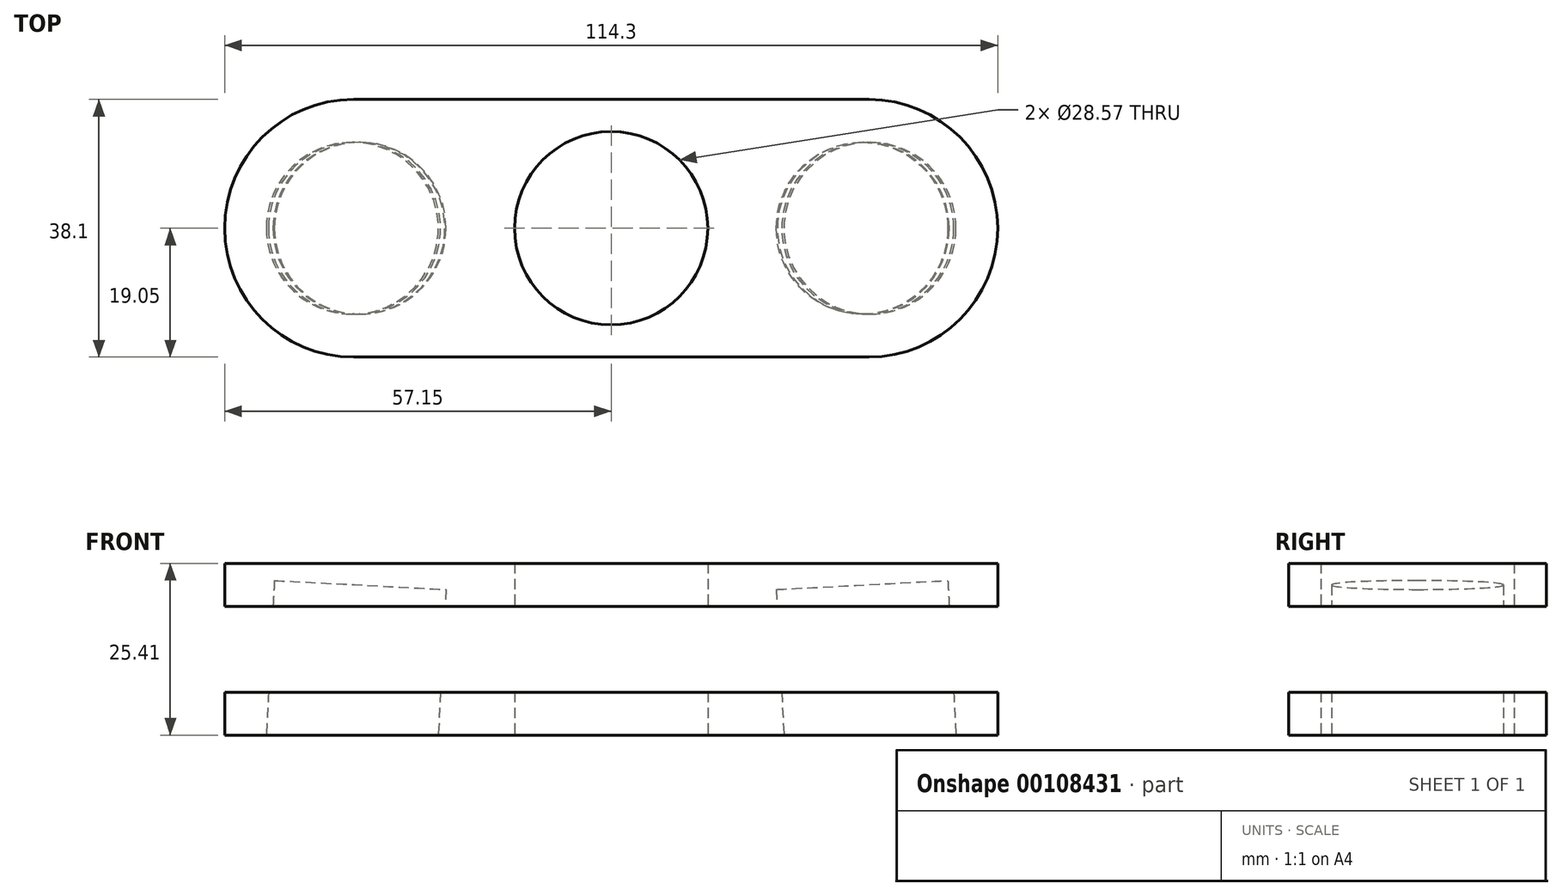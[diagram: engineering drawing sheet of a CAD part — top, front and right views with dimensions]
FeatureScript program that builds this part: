
annotation { "Feature Type Name" : "Feature", "Feature Type Description" : "" }
export const myFeature = defineFeature(function(context is Context, id is Id, definition is map)
    precondition{}
    {
        {
            var Q0;
            Q0=qCreatedBy(makeId("Top.planeOp"),FACE);
            var sketch = newSketch(context, id + "F0", { "sketchPlane" : qUnion([Q0])});
            skLineSegment(sketch, "E0.bottom", {"start": v(38.1, 19.05) * mm, "end": v(-38.1, 19.05) * mm});
            skLineSegment(sketch, "E0.top", {"start": v(38.1, -19.05) * mm, "end": v(-38.1, -19.05) * mm});
            skPoint(sketch, "E0.middle", {"position": v(0, 0) * mm});
            skArc(sketch, "E1", {"start": v(38.1, -19.05) * mm, "mid": v(57.15, 0) * mm, "end": v(38.1, 19.05) * mm});
            skArc(sketch, "E2", {"start": v(-38.1, 19.05) * mm, "mid": v(-57.15, 0) * mm, "end": v(-38.1, -19.05) * mm});
            skCircle(sketch, "E3", {"center": v(0, 0) * mm, "radius": 14.29 * mm});
            skSolve(sketch);
        }
        {
            var Q0;
            Q0 = qSketchRegion(id + "F0", true);
            extrude(context, id + "F1", {"entities" : qUnion([Q0]), "depth" : 6.35 * mm, "symmetric" : true});
        }
        {
            var Q0;
            Q0=qCreatedBy(makeId("Top.planeOp"),FACE);
            var sketch = newSketch(context, id + "F2", { "sketchPlane" : qUnion([Q0])});
            skLineSegment(sketch, "E4.bottom", {"start": v(38.1, 19.05) * mm, "end": v(-38.1, 19.05) * mm});
            skLineSegment(sketch, "E4.top", {"start": v(38.1, -19.05) * mm, "end": v(-38.1, -19.05) * mm});
            skPoint(sketch, "E4.middle", {"position": v(0, 0) * mm});
            skArc(sketch, "E5", {"start": v(38.1, -19.05) * mm, "mid": v(57.15, 0) * mm, "end": v(38.1, 19.05) * mm});
            skArc(sketch, "E6", {"start": v(-38.1, 19.05) * mm, "mid": v(-57.15, 0) * mm, "end": v(-38.1, -19.05) * mm});
            skCircle(sketch, "E7", {"center": v(0, 0) * mm, "radius": 14.29 * mm});
            skLineSegment(sketch, "E8", {"start": v(-38.1, -19.05) * mm, "end": v(-38.1, 19.05) * mm});
            skSolve(sketch);
        }
        {
            var Q0;
            Q0 = qSketchRegion(id + "F2", true);
            var Q1;
            {var subQ0=sQuery(id+"F2.wireOp",EDGE,"dc2b3e3d-155e-4a51-b2ac-76b190b46172");var subQ1=sQuery(id+"F2.wireOp",EDGE,"E4.left");var subQ2=makeQuery(id+"F2.imprint","INTERSECT",VERTEX,{"disambiguationData":[OD(0.0)],"derivedFrom":[subQ1,subQ0]});Q1=makeQuery(id+"F2.imprint","IMPRINT",FACE,{"disambiguationData":[TD([[makeQuery(id+"F2.imprint","IMPRINT",EDGE,{"disambiguationData":[TD([[subQ2,-1.0]])],"derivedFrom":subQ1}),-1.0]])]});}
            var Q2;
            {var subQ0=sQuery(id+"F2.wireOp",EDGE,"dc2b3e3d-155e-4a51-b2ac-76b190b46172");var subQ1=sQuery(id+"F2.wireOp",EDGE,"E4.left");var subQ2=makeQuery(id+"F2.imprint","INTERSECT",VERTEX,{"disambiguationData":[OD(0.0)],"derivedFrom":[subQ1,subQ0]});Q2=makeQuery(id+"F2.imprint","IMPRINT",FACE,{"disambiguationData":[TD([[makeQuery(id+"F2.imprint","IMPRINT",EDGE,{"disambiguationData":[TD([[subQ2,-1.0]])],"derivedFrom":subQ1}),1.0]])]});}
            var Q3;
            {var subQ0=sQuery(id+"F2.wireOp",EDGE,"c2caedd5-78f3-4b19-bee0-835ddcbc3972");var subQ1=sQuery(id+"F2.wireOp",EDGE,"E4.right");var subQ2=makeQuery(id+"F2.imprint","INTERSECT",VERTEX,{"disambiguationData":[OD(0.0)],"derivedFrom":[subQ1,subQ0]});Q3=makeQuery(id+"F2.imprint","IMPRINT",FACE,{"disambiguationData":[TD([[makeQuery(id+"F2.imprint","IMPRINT",EDGE,{"disambiguationData":[TD([[subQ2,-1.0]])],"derivedFrom":subQ1}),1.0]])]});}
            var Q4;
            {var subQ0=sQuery(id+"F2.wireOp",EDGE,"c2caedd5-78f3-4b19-bee0-835ddcbc3972");var subQ1=sQuery(id+"F2.wireOp",EDGE,"E4.right");var subQ2=makeQuery(id+"F2.imprint","INTERSECT",VERTEX,{"disambiguationData":[OD(0.0)],"derivedFrom":[subQ1,subQ0]});Q4=makeQuery(id+"F2.imprint","IMPRINT",FACE,{"disambiguationData":[TD([[makeQuery(id+"F2.imprint","IMPRINT",EDGE,{"disambiguationData":[TD([[subQ2,-1.0]])],"derivedFrom":subQ1}),-1.0]])]});}
            extrude(context, id + "F3", {"entities" : qUnion([Q0, Q1, Q2, Q3, Q4]), "depth" : 6.35 * mm, "symmetric" : true});
        }
        {
            var Q0;
            Q0=qCreatedBy(makeId("Front.planeOp"),FACE);
            var sketch = newSketch(context, id + "F4", { "sketchPlane" : qUnion([Q0])});
            skLineSegment(sketch, "E9", {"start": v(0, -19.05) * mm, "end": v(0, 0) * mm});
            skSolve(sketch);
        }
        {
            var Q0;
            Q0=makeQuery(id+"F1.opExtrude","SWEPT_BODY",BODY,{"disambiguationData":[OSD([sQuery(id+"F0.wireOp",EDGE,"E0.bottom"),sQuery(id+"F0.wireOp",EDGE,"E0.top"),sQuery(id+"F0.wireOp",EDGE,"E1"),sQuery(id+"F0.wireOp",EDGE,"E2"),sQuery(id+"F0.wireOp",EDGE,"j2VXzt2y-2g2I-Fy6j-QZJ0-eHgaToXYIojf"),sQuery(id+"F0.wireOp",EDGE,"UyGj8PRT-RWUs-hjYV-orBx-t6ErGKaiEqpx"),sQuery(id+"F0.wireOp",EDGE,"E3")])]});
            var Q1;
            Q1=sQuery(id+"F4.wireOp",EDGE,"E9");
            transform(context, id + "F5", {"entities" : qUnion([Q0]), "transformType" : TransformType.TRANSLATION_ENTITY, "oppositeDirectionEntity" : false, "transformLine" : qUnion([Q1]), "makeCopy" : false});
        }
        {
            var Q0;
            Q0=qCreatedBy(makeId("Top.planeOp"),FACE);
            var sketch = newSketch(context, id + "F6", { "sketchPlane" : qUnion([Q0])});
            skCircle(sketch, "E10", {"center": v(-38.1, 0) * mm, "radius": 12.7 * mm});
            skLineSegment(sketch, "E11", {"start": v(-38.1, 12.7) * mm, "end": v(-38.1, -12.7) * mm});
            skSolve(sketch);
        }
        {
            var Q0;
            Q0=makeQuery(id+"F6.imprint","IMPRINT",FACE,{"disambiguationData":[TD([[makeQuery(id+"F6.imprint","IMPRINT",EDGE,{"derivedFrom":sQuery(id+"F6.wireOp",EDGE,"E10")}),1.0]])]});
            extrude(context, id + "F7", {"entities" : qUnion([Q0]), "depth" : 38.1 * mm, "symmetric" : true});
        }
        {
            var Q0;
            Q0=makeQuery(id+"F7.opExtrude","SWEPT_BODY",BODY,{"disambiguationData":[OSD([sQuery(id+"F6.wireOp",EDGE,"E10")])]});
            var Q1;
            Q1=sQuery(id+"F2.wireOp",EDGE,"E8");
            transform(context, id + "F8", {"entities" : qUnion([Q0]), "transformType" : TransformType.ROTATION, "transformAxis" : qUnion([Q1]), "angle" : 3 * degree, "makeCopy" : false});
        }
        {
            var Q0;
            Q0=makeQuery(id+"F7.opExtrude","SWEPT_BODY",BODY,{"disambiguationData":[OSD([sQuery(id+"F6.wireOp",EDGE,"E10")])]});
            var Q1;
            Q1=qCreatedBy(makeId("Right.planeOp"),FACE);
            mirror(context, id + "F9", {"entities" : qUnion([Q0]), "mirrorPlane" : qUnion([Q1])});
        }
        {
            var Q0;
            Q0=makeQuery(id+"F7.opExtrude","SWEPT_BODY",BODY,{"disambiguationData":[OSD([sQuery(id+"F6.wireOp",EDGE,"E10")])]});
            var Q1;
            Q1=makeQuery(id+"F9.opPattern","COPY",BODY,{"derivedFrom":makeQuery(id+"F7.opExtrude","SWEPT_BODY",BODY,{"disambiguationData":[OSD([sQuery(id+"F6.wireOp",EDGE,"E10")])]}),"instanceName":"1"});
            var Q2;
            Q2=makeQuery(id+"F1.opExtrude","SWEPT_BODY",BODY,{"disambiguationData":[OSD([sQuery(id+"F0.wireOp",EDGE,"E0.bottom"),sQuery(id+"F0.wireOp",EDGE,"E0.top"),sQuery(id+"F0.wireOp",EDGE,"E1"),sQuery(id+"F0.wireOp",EDGE,"E2"),sQuery(id+"F0.wireOp",EDGE,"E3")])]});
            var Q3;
            Q3=makeQuery(id+"F3.opExtrude","SWEPT_BODY",BODY,{"disambiguationData":[OSD([sQuery(id+"F2.wireOp",EDGE,"E4.bottom"),sQuery(id+"F2.wireOp",EDGE,"E4.top"),sQuery(id+"F2.wireOp",EDGE,"E5"),sQuery(id+"F2.wireOp",EDGE,"E6"),sQuery(id+"F2.wireOp",EDGE,"E7")])]});
            booleanBodies(context, id + "F10", {"operationType" : BooleanOperationType.SUBTRACTION, "tools" : qUnion([Q0, Q1]), "targets" : qUnion([Q2, Q3])});
        }
    });
